# Revit family: KL-P-015-iK-R
name_source: partatom
category: HLS-Bauteile
units: mm (PartAtom-declared; Revit-internal decimal feet)

## family parameters
Arbeitsebenenbasiert = Nein
Beim Laden mit Abzugskörper schneiden = Nein
Bemaßung runder Anschluss = Durchmesser verwenden
Gemeinsam genutzt = Nein
Immer vertikal = Ja
Klassifizierung = Keine
Raumberechnungspunkt = Nein
Teiletyp = Normal

## types (1)
- KL-P-015-iK-R
    Außenluftbreite = 220 mm  [stored 0.721785 ft]
    B = 670 mm  [stored 2.19816 ft]
    Fortluftbreite = 220 mm  [stored 0.721785 ft]
    H = 1790 mm  [stored 5.8727 ft]
    Hersteller = Hansa
    L = 1860 mm  [stored 6.10236 ft]
    L1 = 1230 mm  [stored 4.03543 ft]
    L2 = 630 mm  [stored 2.06693 ft]
    Modell = KL-P-015-iK-R
    RLT_Breite = 670 mm  [stored 2.19816 ft]
    RLT_Höhe = 1790 mm  [stored 5.8727 ft]
    RLT_Serie = KL-P-015-iK
    RLT_Volumenstrom_max = 1500 m³/h
    Vorgabe-Ansicht = 0 mm  [stored 0 ft]

note: [stored X ft] marks values corroborated as IEEE doubles in the binary element streams (Revit-internal decimal feet)
